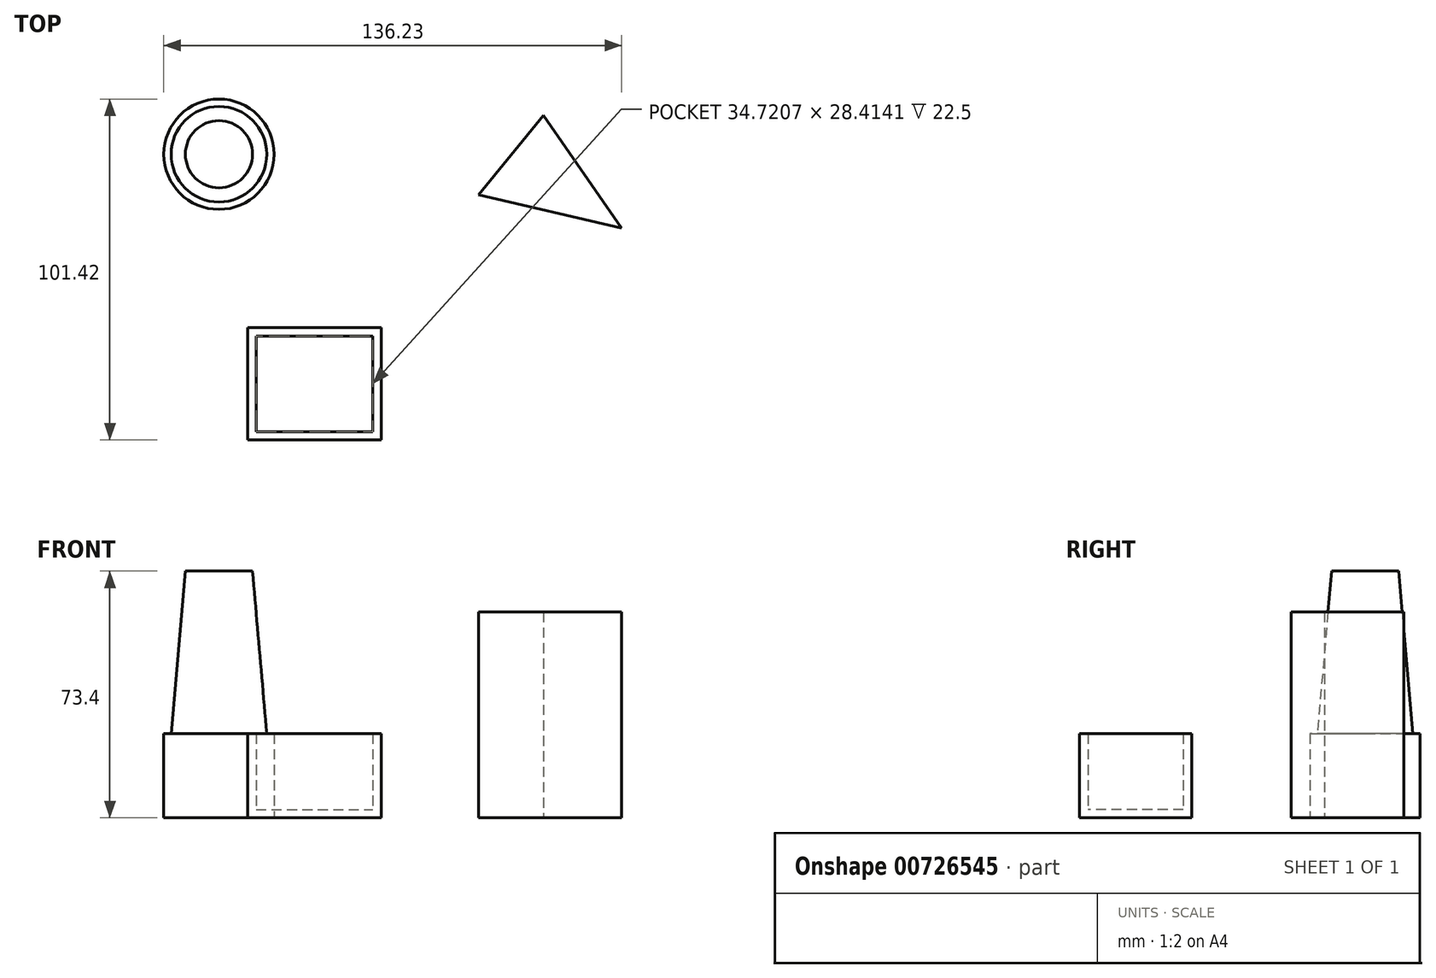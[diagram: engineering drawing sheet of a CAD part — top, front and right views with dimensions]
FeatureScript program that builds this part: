
annotation { "Feature Type Name" : "Feature", "Feature Type Description" : "" }
export const myFeature = defineFeature(function(context is Context, id is Id, definition is map)
    precondition{}
    {
        {
            var Q0;
            Q0=qCreatedBy(makeId("Top.planeOp"),FACE);
            var sketch = newSketch(context, id + "F0", { "sketchPlane" : qUnion([Q0])});
            skCircle(sketch, "E0", {"center": v(-56.76, 47.34) * mm, "radius": 16.4 * mm});
            skLineSegment(sketch, "E1.bottom", {"start": v(-48.23, -4.26) * mm, "end": v(-8.5, -4.26) * mm});
            skLineSegment(sketch, "E1.top", {"start": v(-48.23, -37.67) * mm, "end": v(-8.5, -37.67) * mm});
            skLineSegment(sketch, "E1.left", {"start": v(-48.23, -4.26) * mm, "end": v(-48.23, -37.67) * mm});
            skLineSegment(sketch, "E1.right", {"start": v(-8.5, -4.26) * mm, "end": v(-8.5, -37.67) * mm});
            skLineSegment(sketch, "E2", {"start": v(39.76, 58.87) * mm, "end": v(20.5, 35.26) * mm});
            skLineSegment(sketch, "E3", {"start": v(20.5, 35.26) * mm, "end": v(63.06, 25.32) * mm});
            skLineSegment(sketch, "E4", {"start": v(63.06, 25.32) * mm, "end": v(39.76, 58.87) * mm});
            skSolve(sketch);
        }
        {
            var Q0;
            Q0=makeQuery(id+"F0.imprint","IMPRINT",FACE,{"disambiguationData":[TD([[makeQuery(id+"F0.imprint","IMPRINT",EDGE,{"derivedFrom":sQuery(id+"F0.wireOp",EDGE,"E0")}),1.0]])]});
            extrude(context, id + "F1", {"entities" : qUnion([Q0]), "depth" : 73.4 * mm, "offsetDistance" : 25 * mm, "hasDraft" : true, "draftAngle" : 5 * degree, "draftPullDirection" : true});
        }
        {
            var Q0;
            Q0 = qSketchRegion(id + "F0", true);
            extrude(context, id + "F2", {"entities" : qUnion([Q0]), "operationType" : NewBodyOperationType.ADD, "depth" : 25 * mm, "offsetDistance" : 25 * mm});
        }
        {
            var Q0;
            Q0=makeQuery(id+"F2.opExtrude","CAP_FACE",FACE,{"disambiguationData":[OSD([sQuery(id+"F0.wireOp",EDGE,"E1.bottom"),sQuery(id+"F0.wireOp",EDGE,"E1.top"),sQuery(id+"F0.wireOp",EDGE,"E1.left"),sQuery(id+"F0.wireOp",EDGE,"E1.right")])],"isStart":false});
            shell(context, id + "F3", {"entities" : qUnion([Q0]), "thickness" : 2.5 * mm});
        }
        {
            var Q0;
            Q0=makeQuery(id+"F2.opExtrude","CAP_FACE",FACE,{"disambiguationData":[OSD([sQuery(id+"F0.wireOp",EDGE,"E2"),sQuery(id+"F0.wireOp",EDGE,"E3"),sQuery(id+"F0.wireOp",EDGE,"E4")])],"isStart":false});
            extrude(context, id + "F4", {"entities" : qUnion([Q0]), "operationType" : NewBodyOperationType.ADD, "depth" : 36.2 * mm, "offsetDistance" : 25 * mm});
        }
    });
